# Revit family: Climaver_Access hatch
name_source: partatom
category: Vyústky vzduchotechniky
units: mm (PartAtom-declared; Revit-internal decimal feet)

## family parameters
Bod výpočtu místnosti = Ne
Kóta kulaté spojky = Použít průměr
Ořezat dutým tvarem při načtení = Ne
Sdílené = Ne
Typ dílu = Normální
Vždy vertikální = Ano
Založené na pracovní rovině = Ne

## types (2) — shared parameters
HEIGHT = 200 mm  [stored 0.656168 ft]
Instalation Manual = https://mail.google.com
Komentáře k typům = Glass wool duct boards for air conditioning, ventilation and heating systems. The system allow to make foursquare duct/duct lines (straight duct, elbow, offset, branch etc.) The panel a high density glass wool duct board and is faced on both sides. The outer facing, a robust aluminum facing, acts as a vapor barrier and ensures that the duct is airtight. The inner facing of the duct may be either a reinforced aluminum facing or a woven glass facing.The pre-insulated, self-supporting duct is designed to offer excellent acoustics, excellent thermal performance and a high level of air-tightness, making the system energy efficient. Application as EN 13403, Airtightness: Thermal conductivity λ = 0,032 [W/(m·K)] for T = 10 °C, Class D, Maximum Static pressure: 800 Pa, Maximum air speed: 18 m/s, Maximum temperature of circulating air: 90°C, Maximum external air temperature 60°C, Minimum temperature: – 30˚C, Dimensional stability: Quantities and measured values : <1 %, Duct assembly: exclusive male/female molded shiplap, Water-vapour diffusion resistence: >140 m².h.Pa/mg (from the facing).
Material = <Podle kategorie>
Popis = Access hatch
TYPE = Fitting
URL = https://www.isover-technical-insulation.com
Výrobce = Saint-Gobain - Isove
WIDTH = 300 mm  [stored 0.984252 ft]
zero-valued in all types: Cena, Výchozí výška

## per-type parameters (varying)
| type | Panel thickness |
| 25 mm | 25 mm  [stored 0.082021 ft] |
| 40 mm | 40 mm  [stored 0.131234 ft] |

note: [stored X ft] marks values corroborated as IEEE doubles in the binary element streams (Revit-internal decimal feet)
